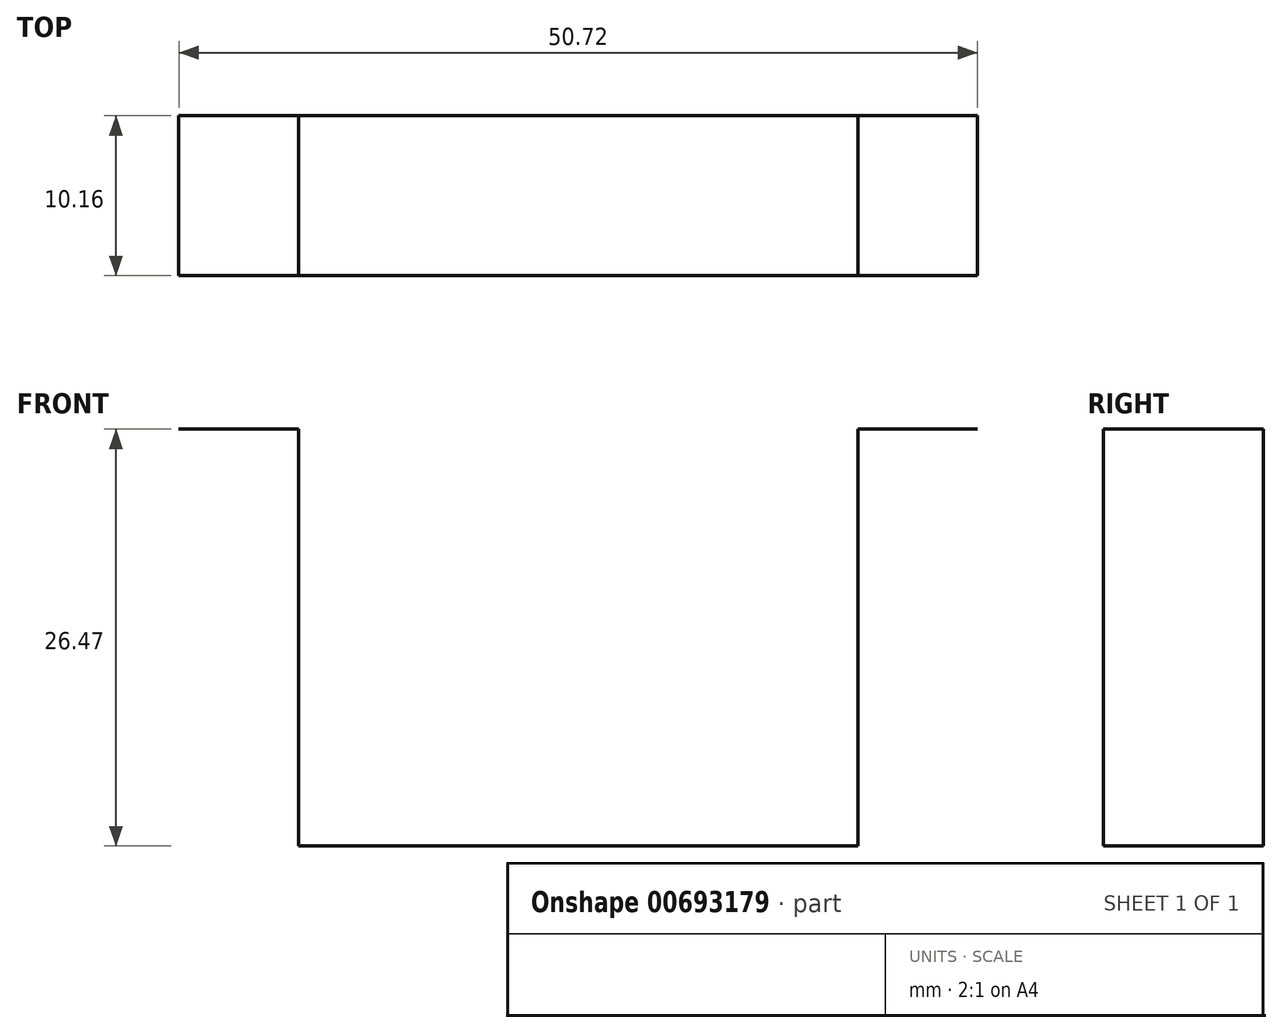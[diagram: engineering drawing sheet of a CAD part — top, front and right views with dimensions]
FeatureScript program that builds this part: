
annotation { "Feature Type Name" : "Feature", "Feature Type Description" : "" }
export const myFeature = defineFeature(function(context is Context, id is Id, definition is map)
    precondition{}
    {
        {
            var Q0;
            Q0=qCreatedBy(makeId("Front.planeOp"),FACE);
            var sketch = newSketch(context, id + "F0", { "sketchPlane" : qUnion([Q0])});
            skLineSegment(sketch, "E0", {"start": v(-25.36, 26.47) * mm, "end": v(-17.77, 26.47) * mm});
            skLineSegment(sketch, "E1", {"start": v(-17.77, 26.47) * mm, "end": v(-17.77, 0) * mm});
            skLineSegment(sketch, "E2", {"start": v(-17.77, 0) * mm, "end": v(0, 0) * mm});
            skLineSegment(sketch, "E3", {"start": v(0, 0) * mm, "end": v(17.77, 0) * mm});
            skLineSegment(sketch, "E4", {"start": v(17.77, 0) * mm, "end": v(17.77, 26.47) * mm});
            skLineSegment(sketch, "E5", {"start": v(17.77, 26.47) * mm, "end": v(25.36, 26.47) * mm});
            skSolve(sketch);
        }
        {
            var Q0;
            Q0=sQuery(id+"F0.wireOp",EDGE,"E0");
            var Q1;
            Q1=sQuery(id+"F0.wireOp",EDGE,"E1");
            var Q2;
            Q2=sQuery(id+"F0.wireOp",EDGE,"E2");
            var Q3;
            Q3=sQuery(id+"F0.wireOp",EDGE,"E3");
            var Q4;
            Q4=sQuery(id+"F0.wireOp",EDGE,"E4");
            var Q5;
            Q5=sQuery(id+"F0.wireOp",EDGE,"E5");
            extrude(context, id + "F1", {"bodyType" : ToolBodyType.SURFACE, "surfaceEntities" : qUnion([Q0, Q1, Q2, Q3, Q4, Q5]), "depth" : 10.16 * mm, "offsetDistance" : 25.4 * mm});
        }
    });
